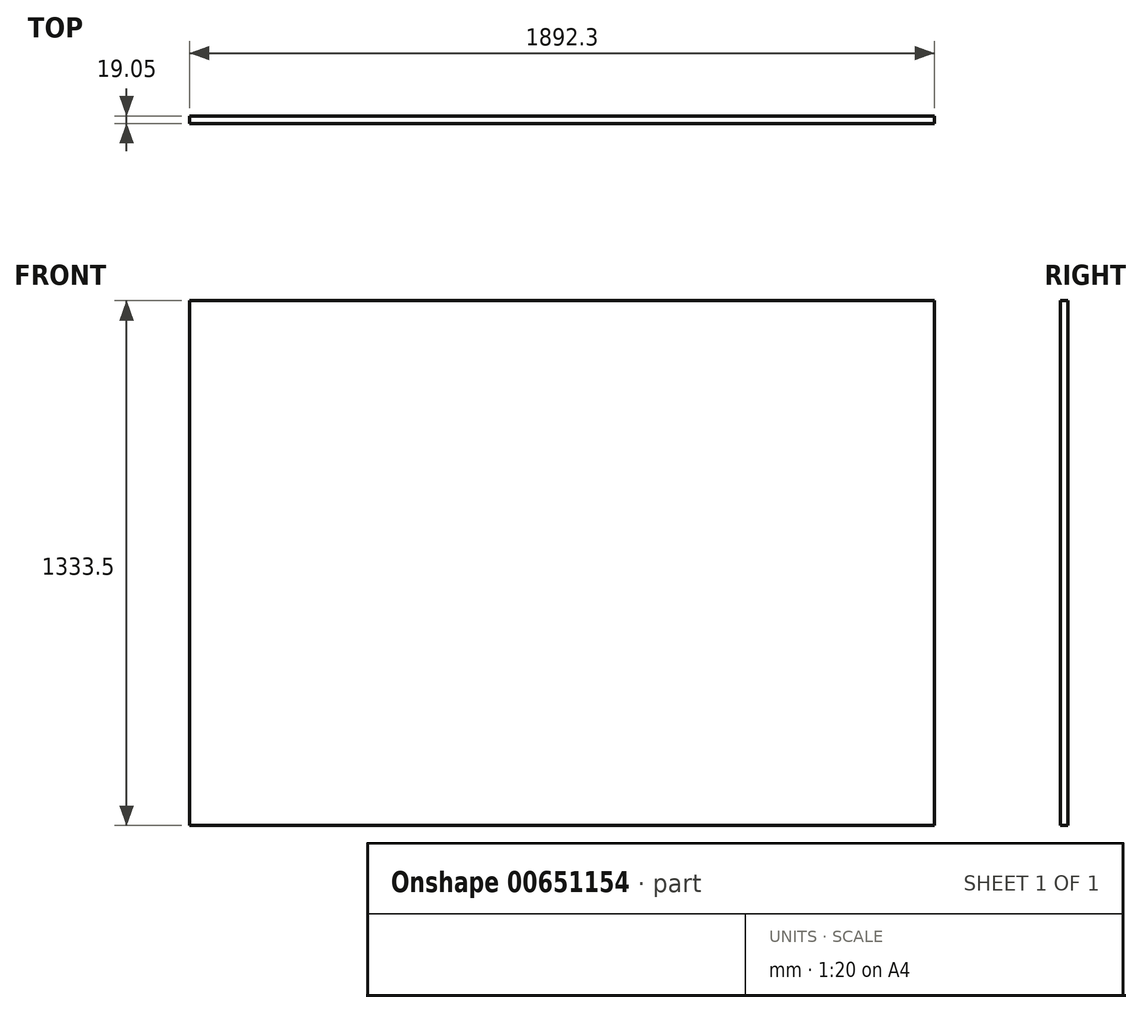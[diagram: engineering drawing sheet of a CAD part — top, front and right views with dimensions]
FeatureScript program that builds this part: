
annotation { "Feature Type Name" : "Feature", "Feature Type Description" : "" }
export const myFeature = defineFeature(function(context is Context, id is Id, definition is map)
    precondition{}
    {
        {
            var Q0;
            Q0=qCreatedBy(makeId("Front.planeOp"),FACE);
            var sketch = newSketch(context, id + "F0", { "sketchPlane" : qUnion([Q0])});
            skLineSegment(sketch, "E0.bottom", {"start": v(946.15, 666.75) * mm, "end": v(-946.15, 666.75) * mm});
            skLineSegment(sketch, "E0.top", {"start": v(946.15, -666.75) * mm, "end": v(-946.15, -666.75) * mm});
            skLineSegment(sketch, "E0.left", {"start": v(946.15, 666.75) * mm, "end": v(946.15, -666.75) * mm});
            skLineSegment(sketch, "E0.right", {"start": v(-946.15, 666.75) * mm, "end": v(-946.15, -666.75) * mm});
            skPoint(sketch, "E0.middle", {"position": v(0, 0) * mm});
            skSolve(sketch);
        }
        {
            var Q0;
            Q0=makeQuery(id+"F0.imprint","IMPRINT",FACE,{"disambiguationData":[TD([[makeQuery(id+"F0.imprint","IMPRINT",EDGE,{"derivedFrom":sQuery(id+"F0.wireOp",EDGE,"E0.bottom")}),1.0]])]});
            extrude(context, id + "F1", {"entities" : qUnion([Q0]), "depth" : 19.05 * mm, "offsetDistance" : 25.4 * mm});
        }
    });
